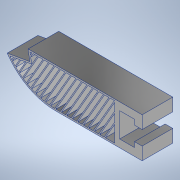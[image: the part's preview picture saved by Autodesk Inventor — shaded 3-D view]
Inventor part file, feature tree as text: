
AUTODESK INVENTOR PART (.ipt)
format: ipt  version: 2022 (Build 260153000, 153)  size: 407,040 bytes
history: native  units: mm
features: extrude x7, sketch x6, fillet x1, shell x1, projected_geometry x1
ambient origin geometry x8: Origin, YZ Plane, XZ Plane, XY Plane, X Axis, Y Axis, Z Axis, Center Point
bodies: Body1 (feature_tree)
feature tree (16):
  extrude  "Extrusion2"  Depth=5.8mm
  extrude  "Extrusion5"  Depth=12.0mm TaperAngle=0.0deg
  fillet  "Fillet2"  Radius=45.0mm
  shell  "Shell1"  Thickness=15.6mm
  extrude  "Extrusion7"  TaperAngle=0.0deg  [1 undecoded]
  extrude  "Extrusion8"  Depth=9.6mm
  extrude  "Extrusion9"  Depth=9.0mm
  extrude  "Extrusion10"  Depth=23.0mm
  extrude  "Extrusion11"  Depth=0.62mm
  sketch  "Sketch5"  dims[d41=5.8mm d48=44.0mm]
  sketch  "Sketch8"  dims[d50=3.0mm d56=12.0mm d57=0.0mm d63=45.0mm d67=15.6mm d71=0.0mm]
  sketch  "Sketch13"  dims[d80=17.453293mm d82=0.0mm d83=0.0mm]
  sketch  "Sketch14"  dims[d87=5.6mm d88=9.6mm]
  projected_geometry  "Projected Loop1"
  sketch  "Sketch16"  dims[d95=4.0mm d96=9.0mm]
  sketch  "Sketch17"  dims[d97=15.6mm d98=23.0mm d99=0.62mm d100=12.0mm d101=0.0mm d102=10.747401mm d103=12.0mm d104=0.0mm d105=0.38mm d1=0.38mm d127=12.0mm d128=0.0mm d130=120.0deg d132=120.0deg d133=0.38mm d135=0.38mm d136=0.38mm d137=0.38mm d138=0.38mm d139=0.38mm d140=0.38mm d141=0.38mm d143=0.38mm d152=120.0deg d153=12.0mm d154=0.0mm d155=4.3mm d156=4.3mm d157=4.3mm d158=4.3mm d159=4.3mm d160=4.3mm d161=4.3mm d162=4.3mm d164=4.3mm d165=0.38mm d166=2.15mm d167=2.15mm d168=0.38mm d169=0.38mm d170=2.15mm d171=0.38mm d172=2.15mm d173=0.38mm d174=2.15mm d176=0.38mm d177=2.15mm d178=0.38mm d180=2.15mm d181=0.38mm d182=2.15mm d184=0.38mm d185=2.15mm d186=2.15mm d187=0.38mm d188=12.0mm d189=0.0mm d190=4.0mm]
note: 1 required parameter value undecoded (feature->parameter linkage not recoverable at this tier; creation-order binding heuristic only, values carry confidence <= 0.55)
